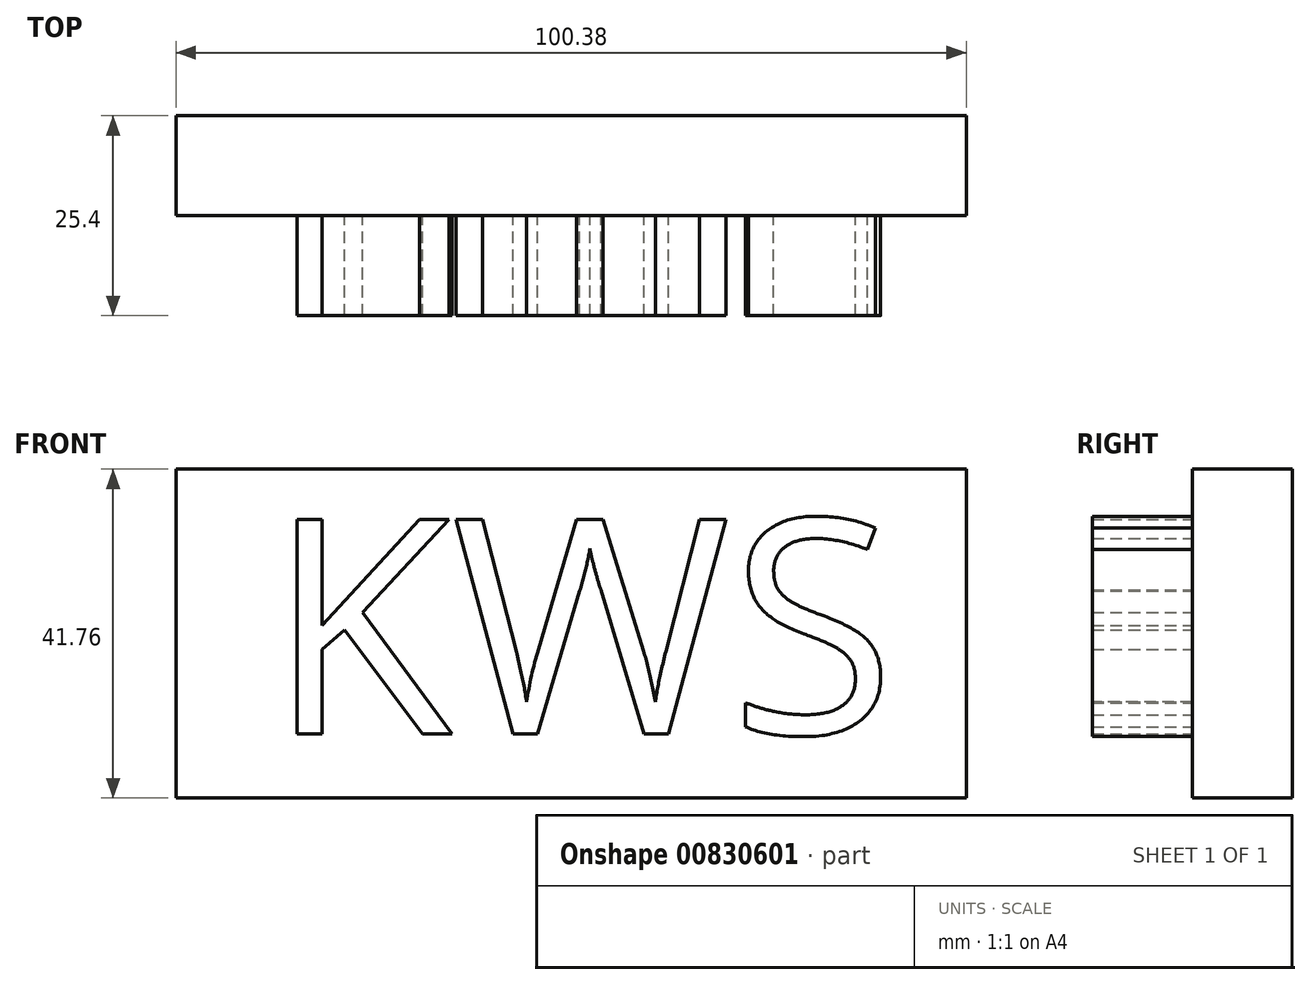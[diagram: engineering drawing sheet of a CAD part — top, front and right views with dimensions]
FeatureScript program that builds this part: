
annotation { "Feature Type Name" : "Feature", "Feature Type Description" : "" }
export const myFeature = defineFeature(function(context is Context, id is Id, definition is map)
    precondition{}
    {
        {
            var Q0;
            Q0=qCreatedBy(makeId("Front.planeOp"),FACE);
            var sketch = newSketch(context, id + "F0", { "sketchPlane" : qUnion([Q0])});
            skLineSegment(sketch, "E0.bottom", {"start": v(0, 0) * mm, "end": v(100.38, 0) * mm});
            skLineSegment(sketch, "E0.top", {"start": v(0, 41.76) * mm, "end": v(100.38, 41.76) * mm});
            skLineSegment(sketch, "E0.left", {"start": v(0, 0) * mm, "end": v(0, 41.76) * mm});
            skLineSegment(sketch, "E0.right", {"start": v(100.38, 0) * mm, "end": v(100.38, 41.76) * mm});
            skSolve(sketch);
        }
        {
            var Q0;
            Q0=makeQuery(id+"F0.imprint","IMPRINT",FACE,{"disambiguationData":[TD([[makeQuery(id+"F0.imprint","IMPRINT",EDGE,{"derivedFrom":sQuery(id+"F0.wireOp",EDGE,"E0.bottom")}),1.0]])]});
            extrude(context, id + "F1", {"entities" : qUnion([Q0]), "depth" : 12.7 * mm, "offsetDistance" : 25.4 * mm});
        }
        {
            var Q0;
            Q0=makeQuery(id+"F1.opExtrude","CAP_FACE",FACE,{"disambiguationData":[OSD([sQuery(id+"F0.wireOp",EDGE,"E0.bottom"),sQuery(id+"F0.wireOp",EDGE,"E0.top"),sQuery(id+"F0.wireOp",EDGE,"E0.left"),sQuery(id+"F0.wireOp",EDGE,"E0.right")])],"isStart":false});
            var sketch = newSketch(context, id + "F2", { "sketchPlane" : qUnion([Q0])});
            skText(sketch, "E1", { "text": "KWS", "fontName": "OpenSans-Regular.ttf"});
            const initialGuessF2  = {"E1": [0.01165, 0.00815, 1, 0, 0.02747]};
            skSetInitialGuess(sketch, initialGuessF2);
            skSolve(sketch);
        }
        {
            var Q0;
            Q0 = qSketchRegion(id + "F2", true);
            extrude(context, id + "F3", {"entities" : qUnion([Q0]), "operationType" : NewBodyOperationType.ADD, "depth" : 12.7 * mm, "offsetDistance" : 25.4 * mm});
        }
    });
